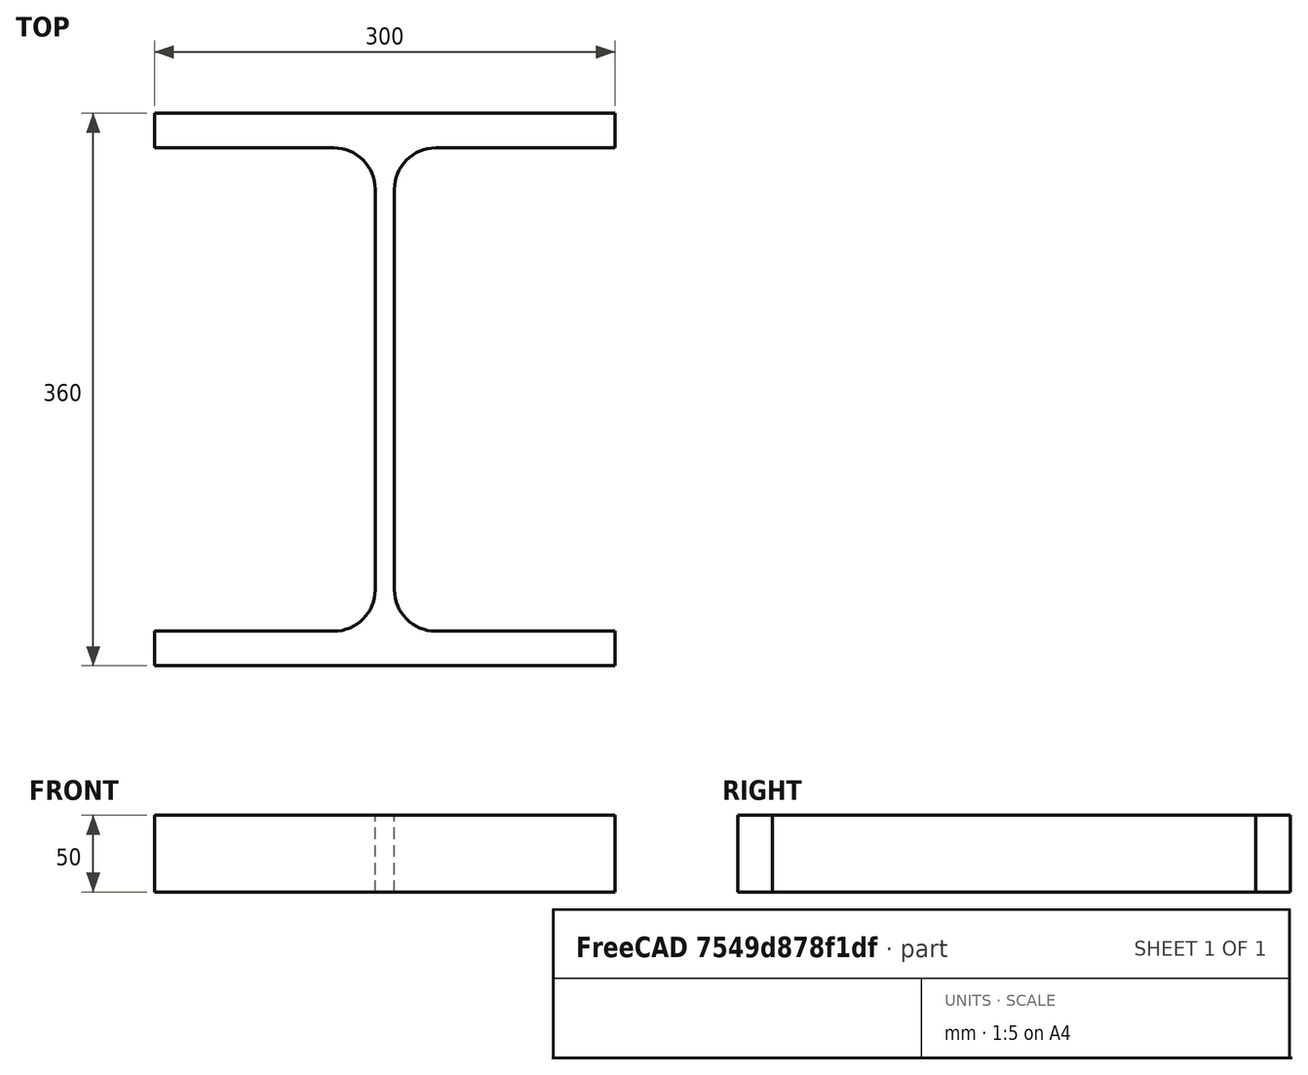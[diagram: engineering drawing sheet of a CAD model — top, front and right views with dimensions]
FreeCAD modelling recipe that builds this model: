
FCSTD DOCUMENT  (FreeCAD 0.15R4671 (Git))
Label: HE-B-Profile 360 DIN1025-2 S235JR
License: All rights reserved
LicenseURL: http://en.wikipedia.org/wiki/All_rights_reserved
objects: Sketcher::SketchObject×1, Part::Extrusion×1
note: 2 computed .brp shape members not serialized (recipe doc carries the construction recipe); baked Part::Feature solids carry a one-line shape summary decoded from their .brp

FEATURE [Sketcher::SketchObject] Sketch
  sketch-geometry (16):
    g0: LineSegment StartX=6.25 StartY=-130.5 StartZ=0 EndX=6.25 EndY=130.5 EndZ=0
    g1: LineSegment StartX=33.25 StartY=157.5 StartZ=0 EndX=150 EndY=157.5 EndZ=0
    g2: LineSegment StartX=150 StartY=157.5 StartZ=0 EndX=150 EndY=180 EndZ=0
    g3: LineSegment StartX=150 StartY=180 StartZ=0 EndX=-150 EndY=180 EndZ=0
    g4: LineSegment StartX=-150 StartY=180 StartZ=0 EndX=-150 EndY=157.5 EndZ=0
    g5: LineSegment StartX=-150 StartY=157.5 StartZ=0 EndX=-33.25 EndY=157.5 EndZ=0
    g6: LineSegment StartX=-6.25 StartY=130.5 StartZ=0 EndX=-6.25 EndY=-130.5 EndZ=0
    g7: LineSegment StartX=-33.25 StartY=-157.5 StartZ=0 EndX=-150 EndY=-157.5 EndZ=0
    g8: LineSegment StartX=-150 StartY=-157.5 StartZ=0 EndX=-150 EndY=-180 EndZ=0
    g9: LineSegment StartX=-150 StartY=-180 StartZ=0 EndX=150 EndY=-180 EndZ=0
    g10: LineSegment StartX=150 StartY=-180 StartZ=0 EndX=150 EndY=-157.5 EndZ=0
    g11: LineSegment StartX=150 StartY=-157.5 StartZ=0 EndX=33.25 EndY=-157.5 EndZ=0
    g12: ArcOfCircle CenterX=33.25 CenterY=130.5 CenterZ=0 NormalX=0 NormalY=0 NormalZ=1 Radius=27 StartAngle=1.5708 EndAngle=3.14159
    g13: ArcOfCircle CenterX=33.25 CenterY=-130.5 CenterZ=0 NormalX=0 NormalY=0 NormalZ=1 Radius=27 StartAngle=3.14159 EndAngle=4.71239
    g14: ArcOfCircle CenterX=-33.25 CenterY=130.5 CenterZ=0 NormalX=0 NormalY=0 NormalZ=1 Radius=27 StartAngle=0 EndAngle=1.5708
    g15: ArcOfCircle CenterX=-33.25 CenterY=-130.5 CenterZ=0 NormalX=0 NormalY=0 NormalZ=1 Radius=27 StartAngle=4.71239 EndAngle=6.28319
  constraints (42):
    c: Vertical(g0)
    c: Coincident(g2,g1)
    c: Vertical(g2)
    c: Coincident(g3,g2)
    c: Coincident(g4,g3)
    c: Vertical(g4)
    c: Coincident(g5,g4)
    c: Horizontal(g5)
    c: Vertical(g6)
    c: Horizontal(g7)
    c: Coincident(g8,g7)
    c: Vertical(g8)
    c: Coincident(g9,g8)
    c: Horizontal(g9)
    c: Coincident(g10,g9)
    c: Vertical(g10)
    c: Coincident(g11,g10)
    c: Horizontal(g11)
    c: Tangent(g1,g12) = 1.5708
    c: Tangent(g0,g12) = 1.5708
    c: Tangent(g0,g13) = 1.5708
    c: Tangent(g11,g13) = 1.5708
    c: Tangent(g5,g14) = 1.5708
    c: Tangent(g6,g14) = 1.5708
    c: Tangent(g6,g15) = 1.5708
    c: Tangent(g7,g15) = 1.5708
    c: Equal(g3,g9)
    c: Equal(g2,g4)
    c: Equal(g4,g8)
    c: Equal(g8,g10)
    c: Equal(g12,g14)
    c: Equal(g14,g15)
    c: Equal(g15,g13)
    c: Symmetric(g2,g3,g-2)
    c: Symmetric(g9,g8,g-2)
    c: Symmetric(g0,g6,g-2)
    c: Symmetric(g2,g9,g-1)
    c: DistanceY(g2,g9) = -360
    c: DistanceX(g3) = -300
    c: DistanceX(g0,g6) = -12.5
    c: DistanceY(g2) = 22.5
    c: Radius(g12) = 27
FEATURE [Part::Extrusion] Extrude  label="HE-B-Profile 360 DIN1025-2 S235JR"
  Base = -> Sketch
  Dir = (0,0,50)
  Solid = true
